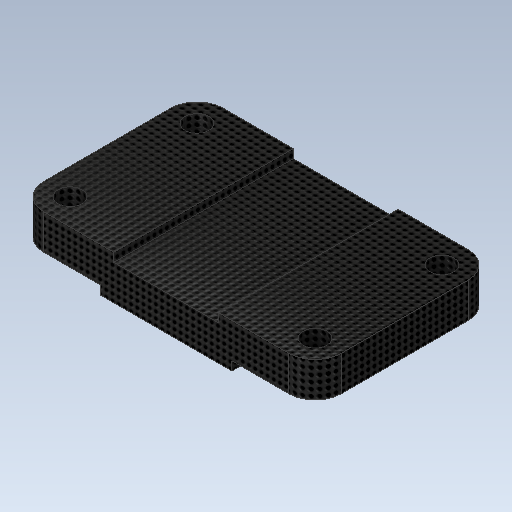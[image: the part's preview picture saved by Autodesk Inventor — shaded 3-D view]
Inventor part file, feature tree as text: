
AUTODESK INVENTOR PART (.ipt)
format: ipt  version: 2020 (Build 240168000, 168)  size: 280,576 bytes
history: native  units: mm
features: extrude x3, sketch x2, fillet x2, mirror x1
ambient origin geometry x8: Origin, YZ Plane, XZ Plane, XY Plane, X Axis, Y Axis, Z Axis, Center Point
bodies: Solid1 (feature_tree)
feature tree (8):
  extrude  "Extrusion1"  Depth=4.0mm
  sketch  "Sketch2"  dims[d2=38.0mm d3=16.0mm d4=44.0mm d5=4.0mm d6=82.0mm d7=0.0mm d8=11.0mm d9=11.0mm d10=12.0mm d11=12.0mm d12=12.0mm d13=12.0mm d14=82.0mm d15=0.0mm d16=82.0mm d17=0.0mm d18=12.0mm d19=12.0mm]
  extrude  "Extrusion2"  Depth=16.0mm
  extrude  "Extrusion3"  Depth=44.0mm
  fillet  "Fillet1"  Radius=4.0mm
  fillet  "Fillet2"  Radius=82.0mm
  mirror  "Mirror1"
  sketch  "Sketch1"  dims[d0=30.0mm d1=4.0mm]
